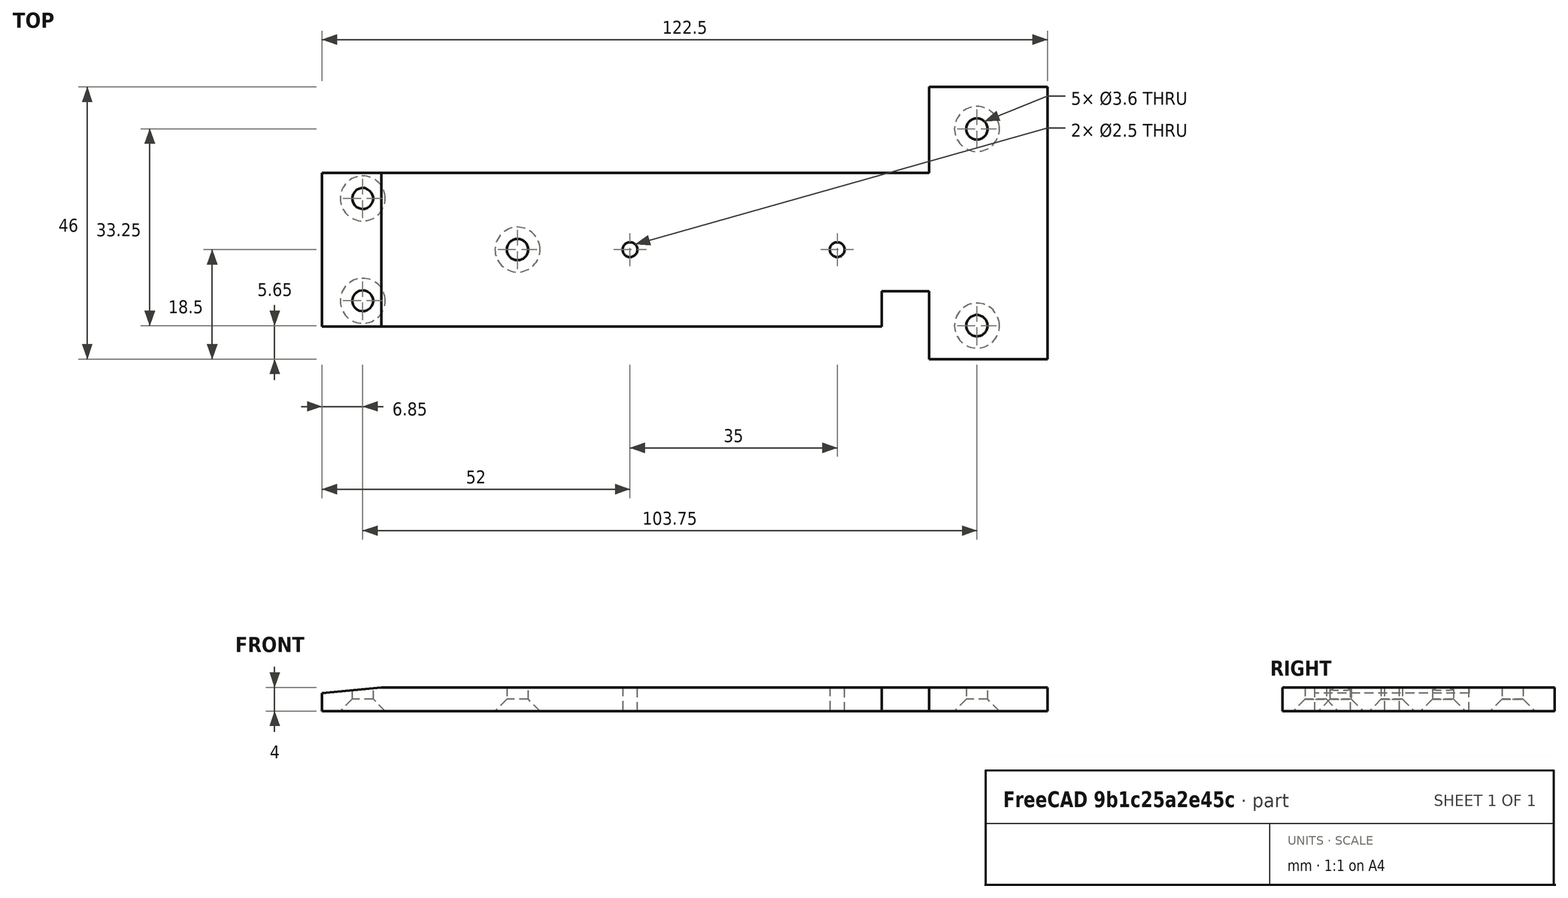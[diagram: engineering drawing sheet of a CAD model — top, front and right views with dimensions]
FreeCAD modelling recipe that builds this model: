
FCSTD DOCUMENT  (FreeCAD 0.18R16146 (Git))
Label: topDeckFront
License: All rights reserved
LicenseURL: http://en.wikipedia.org/wiki/All_rights_reserved
objects: Sketcher::SketchObject×2, Mesh::Feature×1, PartDesign::Pad×1, PartDesign::Pocket×1, PartDesign::Chamfer×1, PartDesign::Body×1
note: 8 computed .brp shape members not serialized (recipe doc carries the construction recipe); baked Part::Feature solids carry a one-line shape summary decoded from their .brp

FEATURE [Mesh::Feature] Top_Deck_Front
FEATURE [Sketcher::SketchObject] Sketch
  MapMode = 5
  Support = -> [XY_Plane]
  sketch-geometry (19):
    g0: LineSegment StartX=-62.66 StartY=13 StartZ=0 EndX=39.84 EndY=13 EndZ=0
    g1: LineSegment StartX=-62.66 StartY=-13 StartZ=0 EndX=-62.66 EndY=13 EndZ=0
    g2: LineSegment StartX=39.84 StartY=27.5 StartZ=0 EndX=59.84 EndY=27.5 EndZ=0
    g3: LineSegment StartX=59.84 StartY=27.5 StartZ=0 EndX=59.84 EndY=-18.5 EndZ=0
    g4: LineSegment StartX=59.84 StartY=-18.5 StartZ=0 EndX=39.84 EndY=-18.5 EndZ=0
    g5: LineSegment StartX=31.84 StartY=-13 StartZ=0 EndX=-62.66 EndY=-13 EndZ=0
    g6: LineSegment StartX=39.84 StartY=13 StartZ=0 EndX=39.84 EndY=27.5 EndZ=0
    g7: Circle CenterX=47.94 CenterY=20.4 CenterZ=0 NormalX=0 NormalY=0 NormalZ=1 AngleXU=0 Radius=1.8
    g8: Circle CenterX=47.94 CenterY=-12.85 CenterZ=0 NormalX=0 NormalY=0 NormalZ=1 AngleXU=0 Radius=1.8
    g9: Circle CenterX=-29.66 CenterY=0 CenterZ=0 NormalX=0 NormalY=0 NormalZ=1 AngleXU=0 Radius=1.8
    g10: Circle CenterX=-55.81 CenterY=8.65 CenterZ=0 NormalX=0 NormalY=0 NormalZ=1 AngleXU=0 Radius=1.8
    g11: Circle CenterX=-55.81 CenterY=-8.65 CenterZ=0 NormalX=0 NormalY=0 NormalZ=1 AngleXU=0 Radius=1.8
    g12: LineSegment [constr] StartX=47.94 StartY=27.5 StartZ=0 EndX=47.94 EndY=-18.5 EndZ=0
    g13: LineSegment [constr] StartX=-55.81 StartY=13 StartZ=0 EndX=-55.81 EndY=-13 EndZ=0
    g14: LineSegment StartX=31.84 StartY=-7 StartZ=0 EndX=39.84 EndY=-7 EndZ=0
    g15: LineSegment StartX=31.84 StartY=-13 StartZ=0 EndX=31.84 EndY=-7 EndZ=0
    g16: LineSegment StartX=39.84 StartY=-7 StartZ=0 EndX=39.84 EndY=-18.5 EndZ=0
    g17: Circle CenterX=-10.66 CenterY=0 CenterZ=0 NormalX=0 NormalY=0 NormalZ=1 AngleXU=0 Radius=1.25
    g18: Circle CenterX=24.34 CenterY=0 CenterZ=0 NormalX=0 NormalY=0 NormalZ=1 AngleXU=0 Radius=1.25
  constraints (59):
    c: Coincident(g5,g1)
    c: Coincident(g1,g0)
    c: Horizontal(g0)
    c: Vertical(g1)
    c: Distance(g1) = 26
    c: DistanceY(g-1,g0) = 13
    c: Coincident(g2,g3)
    c: Coincident(g3,g4)
    c: Coincident(g6,g2)
    c: Horizontal(g2)
    c: Horizontal(g4)
    c: Vertical(g3)
    c: Distance(g2) = 20
    c: Coincident(g6,g0)
    c: DistanceX(g-2,g1) = -62.66
    c: Distance(g3) = 46
    c: DistanceY(g-1,g3) = -18.5
    c: Parallel(g5,g0)
    c: Radius(g7) = 1.8
    c: Distance(g7,g-1) = 20.4
    c: Equal(g7,g8) = 1.8
    c: DistanceY(g-1,g8) = -12.85
    c: Equal(g7,g9) = 1.8
    c: PointOnObject(g9,g-1)
    c: Distance(g9,g1) = 33
    c: PointOnObject(g12,g2)
    c: PointOnObject(g12,g4)
    c: Vertical(g12)
    c: PointOnObject(g7,g12)
    c: PointOnObject(g8,g12)
    c: Distance(g12,g3) = 11.9
    c: PointOnObject(g13,g0)
    c: PointOnObject(g13,g5)
    c: Vertical(g13)
    c: PointOnObject(g10,g13)
    c: PointOnObject(g11,g13)
    c: Distance(g10,g0) = 4.35
    c: Distance(g13,g1) = 6.85
    c: Distance(g11,g5) = 4.35
    c: Equal(g10,g7)
    c: Equal(g11,g7)
    c: Coincident(g15,g14)
    c: Horizontal(g14)
    c: Vertical(g15)
    c: Coincident(g5,g15)
    c: Distance(g14) = 8
    c: Distance(g15) = 6
    c: Coincident(g16,g14)
    c: Coincident(g16,g4)
    c: Vertical(g16)
    c: Distance(g0) = 102.5
    c: Parallel(g6,g16)
    c: PointOnObject(g17,g-1)
    c: Radius(g17) = 1.25
    c: Equal(g17,g18) = 1.25
    c: PointOnObject(g18,g-1)
    c: Distance(g17,g18) = 35
    c: Distance(g4) = 20
    c: Distance(g18,g15) = 7.5
FEATURE [PartDesign::Pad] Pad
  Length = 4
  Length2 = 100
  Profile = -> Sketch
  Type = 0
FEATURE [Sketcher::SketchObject] Sketch001
  MapMode = 5
  Placement = pos=(0,13,0) rot=(0,0.707107,0.707107;3.14159rad)
  sketch-geometry (3):
    g0: LineSegment StartX=62.66 StartY=4 StartZ=0 EndX=52.66 EndY=4 EndZ=0
    g1: LineSegment StartX=62.66 StartY=4 StartZ=0 EndX=62.66 EndY=3 EndZ=0
    g2: LineSegment StartX=52.66 StartY=4 StartZ=0 EndX=62.66 EndY=3 EndZ=0
  constraints (6):
    c: Horizontal(g0)
    c: Coincident(g1,g0)
    c: Coincident(g2,g0)
    c: Coincident(g2,g1)
    c: Distance(g1) = 1
    c: Distance(g0) = 10
FEATURE [PartDesign::Pocket] Pocket
  BaseFeature = -> Pad
  Length = 0
  Length2 = 100
  Profile = -> Sketch001
  Type = 1
FEATURE [PartDesign::Chamfer] Chamfer
  Base = -> Pocket [Edge16,Edge17,Edge15,Edge18,Edge19]
  BaseFeature = -> Pocket
  Size = 2
FEATURE [PartDesign::Body] Body
  Group = -> [Sketch,Pad,Sketch001,Pocket,Chamfer]
  Origin = -> Origin
  Tip = -> Chamfer
